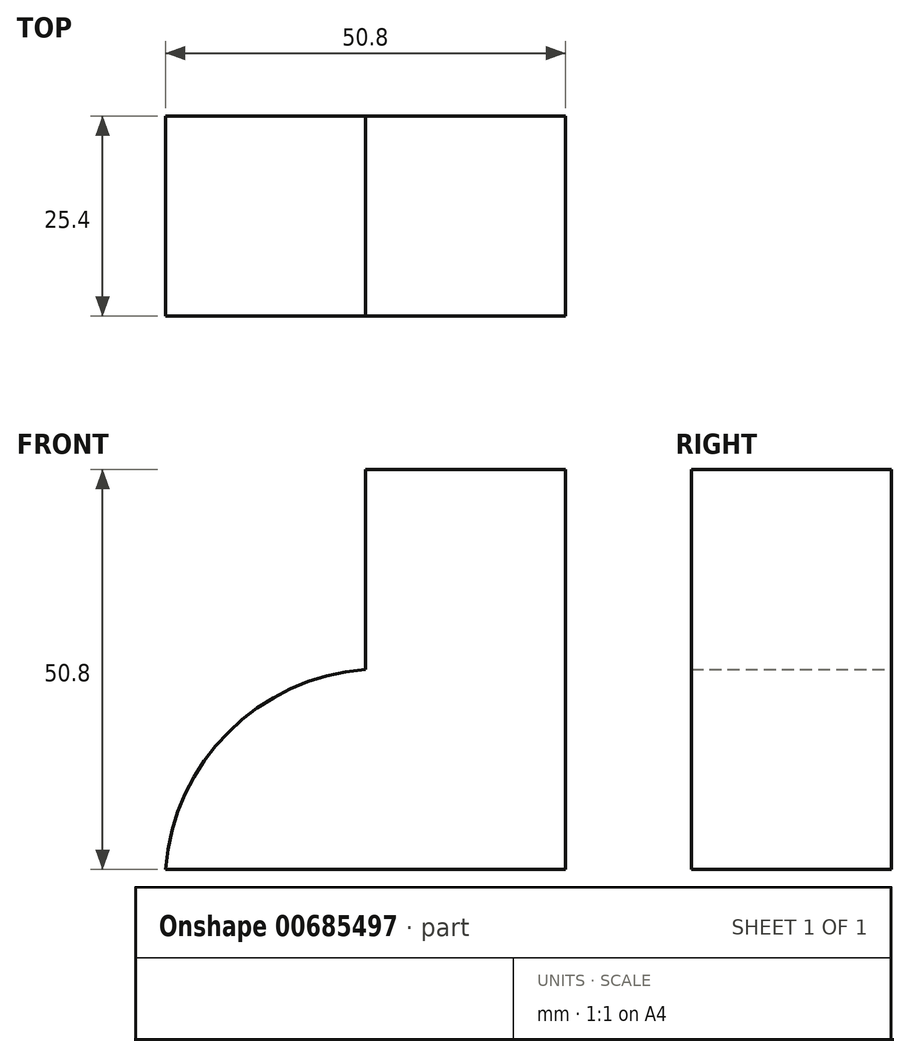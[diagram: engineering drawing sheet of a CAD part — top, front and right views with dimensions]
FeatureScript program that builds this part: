
annotation { "Feature Type Name" : "Feature", "Feature Type Description" : "" }
export const myFeature = defineFeature(function(context is Context, id is Id, definition is map)
    precondition{}
    {
        {
            var Q0;
            Q0=qCreatedBy(makeId("Front.planeOp"),FACE);
            var sketch = newSketch(context, id + "F0", { "sketchPlane" : qUnion([Q0])});
            skLineSegment(sketch, "E0", {"start": v(-39.05, 22.05) * mm, "end": v(-39.05, 47.45) * mm});
            skLineSegment(sketch, "E1", {"start": v(-39.05, 47.45) * mm, "end": v(-13.65, 47.45) * mm});
            skLineSegment(sketch, "E2", {"start": v(-13.65, 47.45) * mm, "end": v(-13.65, -3.35) * mm});
            skLineSegment(sketch, "E3", {"start": v(-13.65, -3.35) * mm, "end": v(-64.45, -3.35) * mm});
            skArc(sketch, "E4", {"start": v(-39.05, 22.05) * mm, "mid": v(-56.48, 14.08) * mm, "end": v(-64.45, -3.35) * mm});
            skSolve(sketch);
        }
        {
            var Q0;
            Q0 = qSketchRegion(id + "F0", true);
            extrude(context, id + "F1", {"entities" : qUnion([Q0]), "depth" : 25.4 * mm, "offsetDistance" : 25.4 * mm});
        }
    });
